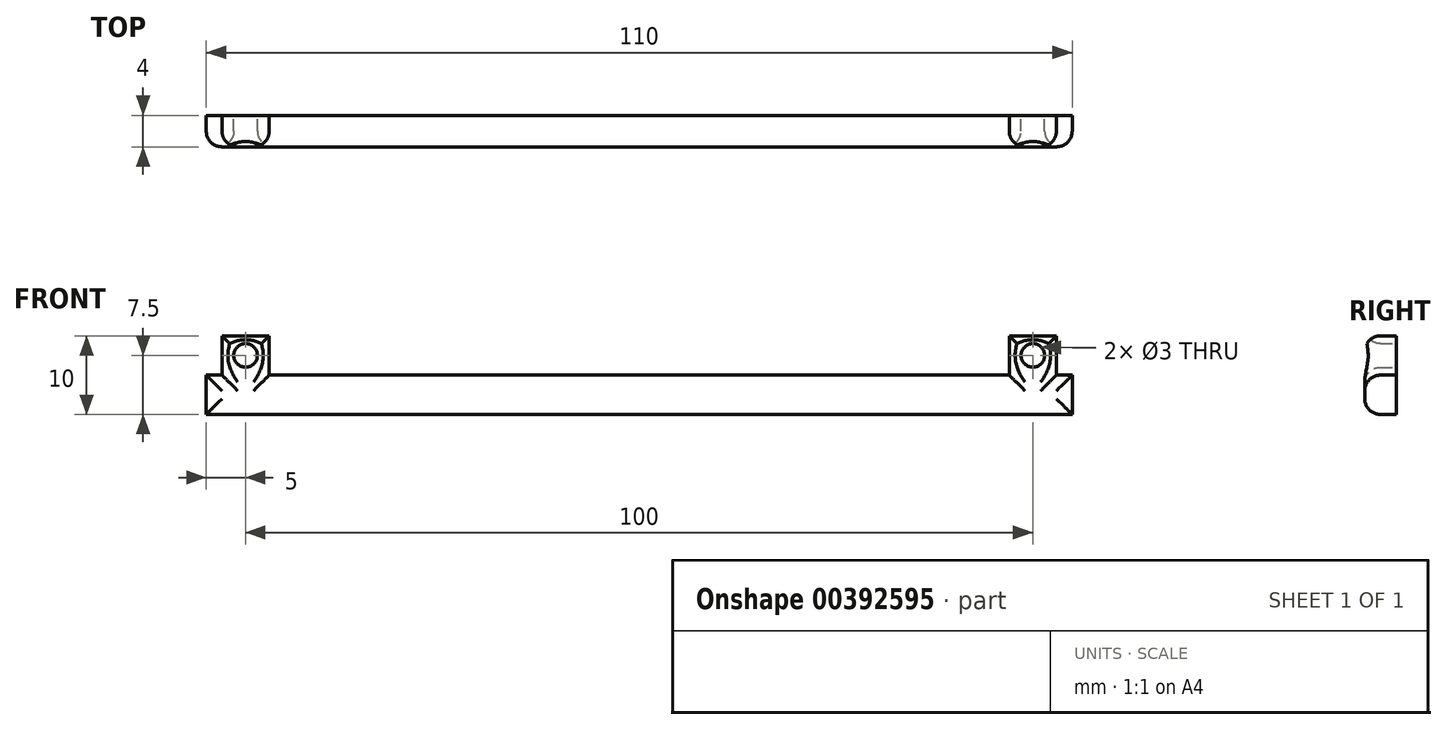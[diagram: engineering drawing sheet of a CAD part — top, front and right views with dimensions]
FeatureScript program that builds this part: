
annotation { "Feature Type Name" : "Feature", "Feature Type Description" : "" }
export const myFeature = defineFeature(function(context is Context, id is Id, definition is map)
    precondition{}
    {
        {
            var Q0;
            Q0=qCreatedBy(makeId("Front.planeOp"),FACE);
            var sketch = newSketch(context, id + "F0", { "sketchPlane" : qUnion([Q0])});
            skLineSegment(sketch, "E0", {"start": v(-55, 0) * mm, "end": v(55, 0) * mm});
            skLineSegment(sketch, "E1", {"start": v(55, 0) * mm, "end": v(55, 5) * mm});
            skLineSegment(sketch, "E2", {"start": v(55, 5) * mm, "end": v(53, 5) * mm});
            skLineSegment(sketch, "E3", {"start": v(53, 5) * mm, "end": v(53, 10) * mm});
            skLineSegment(sketch, "E4", {"start": v(53, 10) * mm, "end": v(47, 10) * mm});
            skLineSegment(sketch, "E5", {"start": v(47, 10) * mm, "end": v(47, 5) * mm});
            skLineSegment(sketch, "E6", {"start": v(47, 5) * mm, "end": v(-47, 5) * mm});
            skLineSegment(sketch, "E7", {"start": v(-47, 5) * mm, "end": v(-47, 10) * mm});
            skLineSegment(sketch, "E8", {"start": v(-47, 10) * mm, "end": v(-53, 10) * mm});
            skLineSegment(sketch, "E9", {"start": v(-53, 10) * mm, "end": v(-53, 5) * mm});
            skLineSegment(sketch, "E10", {"start": v(-53, 5) * mm, "end": v(-55, 5) * mm});
            skLineSegment(sketch, "E11", {"start": v(-55, 5) * mm, "end": v(-55, 0) * mm});
            skCircle(sketch, "E12", {"center": v(-50, 7.5) * mm, "radius": 1.5 * mm});
            skCircle(sketch, "E13.1.0.0", {"center": v(50, 7.5) * mm, "radius": 1.5 * mm});
            skLineSegment(sketch, "E13.direction1", {"start": v(-50, 7.5) * mm, "end": v(50, 7.5) * mm, "construction": true});
            skSolve(sketch);
        }
        {
            var Q0;
            Q0=makeQuery(id+"F0.imprint","IMPRINT",FACE,{"disambiguationData":[TD([[makeQuery(id+"F0.imprint","IMPRINT",EDGE,{"derivedFrom":sQuery(id+"F0.wireOp",EDGE,"E0")}),1.0]])]});
            extrude(context, id + "F1", {"entities" : qUnion([Q0]), "depth" : 4 * mm});
        }
        {
            var Q0;
            Q0=makeQuery(id+"F1.opExtrude","CAP_FACE",FACE,{"disambiguationData":[OSD([sQuery(id+"F0.wireOp",EDGE,"E0"),sQuery(id+"F0.wireOp",EDGE,"E1"),sQuery(id+"F0.wireOp",EDGE,"E2"),sQuery(id+"F0.wireOp",EDGE,"E3"),sQuery(id+"F0.wireOp",EDGE,"E4"),sQuery(id+"F0.wireOp",EDGE,"E5"),sQuery(id+"F0.wireOp",EDGE,"E6"),sQuery(id+"F0.wireOp",EDGE,"E7"),sQuery(id+"F0.wireOp",EDGE,"E8"),sQuery(id+"F0.wireOp",EDGE,"E9"),sQuery(id+"F0.wireOp",EDGE,"E10"),sQuery(id+"F0.wireOp",EDGE,"E11"),sQuery(id+"F0.wireOp",EDGE,"E12"),sQuery(id+"F0.wireOp",EDGE,"E13.1.0.0")])],"isStart":false});
            fillet(context, id + "F2", {"entities" : qUnion([Q0]), "radius" : 2 * mm, "tangentPropagation" : true, "allowEdgeOverflow" : false});
        }
    });
